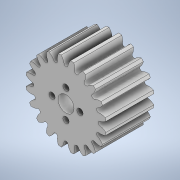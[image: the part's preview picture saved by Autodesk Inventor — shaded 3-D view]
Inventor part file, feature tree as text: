
AUTODESK INVENTOR PART (.ipt)
format: ipt  version: 2021 (Build 250183000, 183)  size: 246,784 bytes
history: native  units: mm
features: extrude x3, sketch x2, pattern_circular x1
ambient origin geometry x8: Origin, YZ Plane, XZ Plane, XY Plane, X Axis, Y Axis, Z Axis, Center Point
bodies: Solid1 (feature_tree)
feature tree (6):
  sketch  "Sketch1"  dims[d0=24.0mm d1=0.0mm]
  extrude  "Extrusion1"  TaperAngle=0.0deg  [1 undecoded]
  extrude  "Extrusion2"  Depth=7.0mm TaperAngle=360.0deg
  pattern_circular  "Circular Pattern1"  [2 undecoded]
  extrude  "Extrusion3"  Depth=7.0mm
  sketch  "Sketch2"  dims[d2=0.0mm d3=0.0mm d4=200.0mm d5=360.0deg d7=8.0mm d8=3.1mm d9=7.0mm d10=40.0mm d12=360.0deg d14=0.0mm d15=0.0mm]
note: 3 required parameter values undecoded (feature->parameter linkage not recoverable at this tier; creation-order binding heuristic only, values carry confidence <= 0.55)
